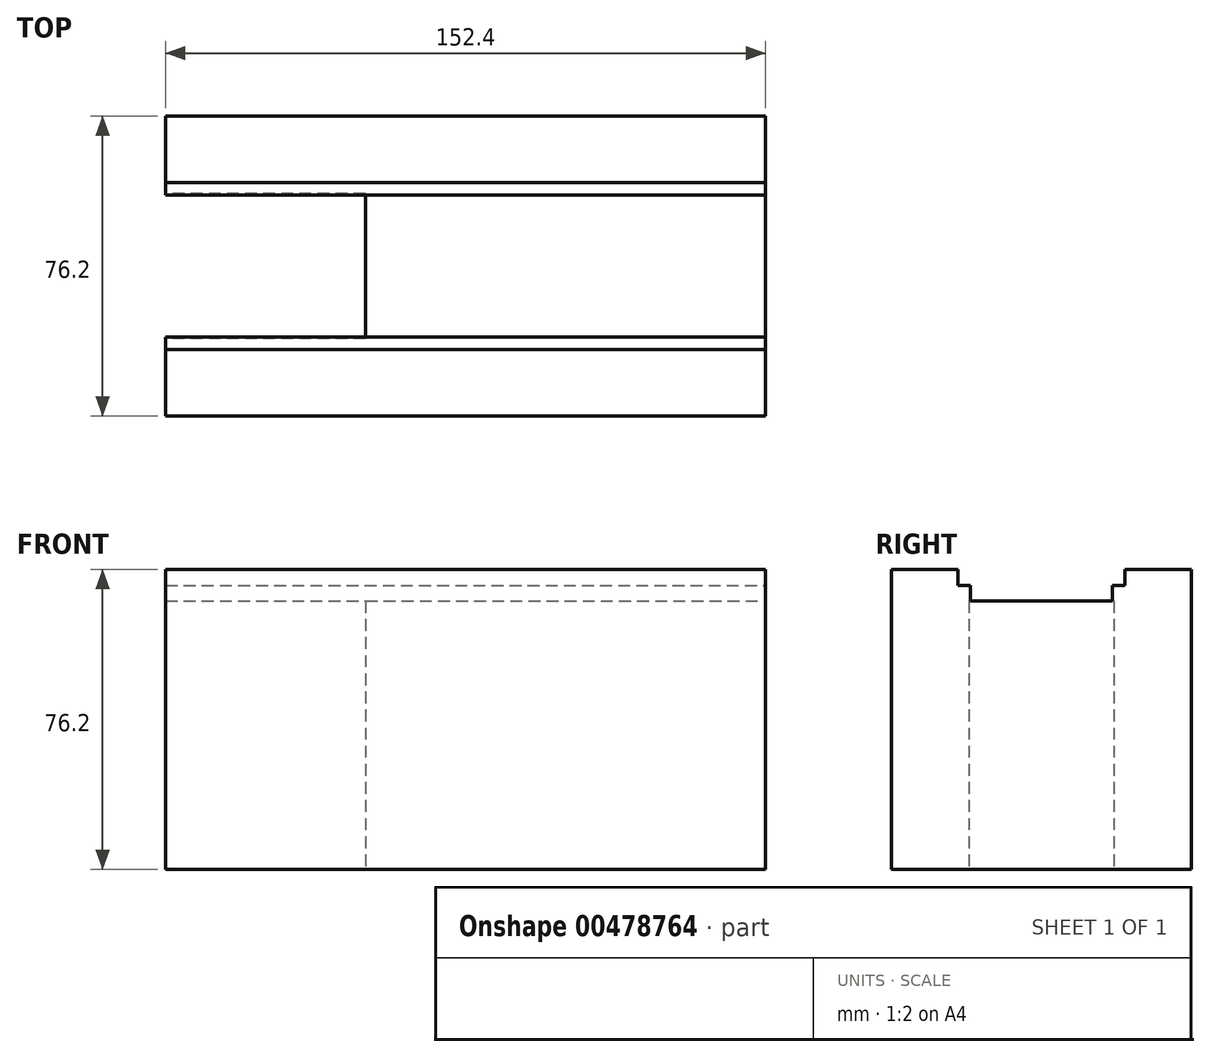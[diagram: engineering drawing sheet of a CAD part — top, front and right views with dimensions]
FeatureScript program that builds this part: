
annotation { "Feature Type Name" : "Feature", "Feature Type Description" : "" }
export const myFeature = defineFeature(function(context is Context, id is Id, definition is map)
    precondition{}
    {
        {
            var Q0;
            Q0=qCreatedBy(makeId("Right.planeOp"),FACE);
            var sketch = newSketch(context, id + "F0", { "sketchPlane" : qUnion([Q0])});
            skLineSegment(sketch, "E0.bottom", {"start": v(0, 0) * mm, "end": v(76.2, 0) * mm});
            skLineSegment(sketch, "E0.top", {"start": v(0, 76.2) * mm, "end": v(76.2, 76.2) * mm});
            skLineSegment(sketch, "E0.left", {"start": v(0, 0) * mm, "end": v(0, 76.2) * mm});
            skLineSegment(sketch, "E0.right", {"start": v(76.2, 0) * mm, "end": v(76.2, 76.2) * mm});
            skSolve(sketch);
        }
        {
            var Q0;
            Q0 = qSketchRegion(id + "F0", true);
            extrude(context, id + "F1", {"entities" : qUnion([Q0]), "depth" : 152.4 * mm});
        }
        {
            var Q0;
            Q0=makeQuery(id+"F1.opExtrude","CAP_FACE",FACE,{"disambiguationData":[OSD([sQuery(id+"F0.wireOp",EDGE,"E0.bottom"),sQuery(id+"F0.wireOp",EDGE,"E0.top"),sQuery(id+"F0.wireOp",EDGE,"E0.left"),sQuery(id+"F0.wireOp",EDGE,"E0.right")])],"isStart":false});
            var sketch = newSketch(context, id + "F2", { "sketchPlane" : qUnion([Q0])});
            skLineSegment(sketch, "E1.top", {"start": v(20.07, 68.2) * mm, "end": v(56.13, 68.2) * mm});
            skLineSegment(sketch, "E1.left", {"start": v(20.07, 76.2) * mm, "end": v(20.07, 68.2) * mm});
            skLineSegment(sketch, "E1.right", {"start": v(56.13, 76.2) * mm, "end": v(56.13, 68.2) * mm});
            skPoint(sketch, "E2", {"position": v(38.1, 68.2) * mm});
            skPoint(sketch, "E3", {"position": v(38.1, 76.2) * mm});
            skSolve(sketch);
        }
        {
            var Q0;
            Q0=makeQuery(id+"F2.imprint","IMPRINT",FACE,{"disambiguationData":[TD([[makeQuery(id+"F2.imprint","IMPRINT",EDGE,{"derivedFrom":sQuery(id+"F2.wireOp",EDGE,"E1.top")}),1.0]])]});
            extrude(context, id + "F3", {"entities" : qUnion([Q0]), "operationType" : NewBodyOperationType.REMOVE, "endBound" : BoundingType.THROUGH_ALL, "oppositeDirection" : true, "depth" : 152.4 * mm});
        }
        {
            var Q0;
            Q0=makeQuery(id+"F1.opExtrude","CAP_FACE",FACE,{"disambiguationData":[OSD([sQuery(id+"F0.wireOp",EDGE,"E0.bottom"),sQuery(id+"F0.wireOp",EDGE,"E0.top"),sQuery(id+"F0.wireOp",EDGE,"E0.left"),sQuery(id+"F0.wireOp",EDGE,"E0.right")])],"isStart":false});
            var sketch = newSketch(context, id + "F4", { "sketchPlane" : qUnion([Q0])});
            skLineSegment(sketch, "E4.bottom", {"start": v(16.9, 76.2) * mm, "end": v(20.07, 76.2) * mm});
            skLineSegment(sketch, "E4.top", {"start": v(16.9, 72.2) * mm, "end": v(20.07, 72.2) * mm});
            skLineSegment(sketch, "E4.left", {"start": v(16.9, 76.2) * mm, "end": v(16.9, 72.2) * mm});
            skLineSegment(sketch, "E4.right", {"start": v(20.07, 76.2) * mm, "end": v(20.07, 72.2) * mm});
            skLineSegment(sketch, "E5.bottom", {"start": v(56.13, 76.2) * mm, "end": v(59.3, 76.2) * mm});
            skLineSegment(sketch, "E5.top", {"start": v(56.13, 72.2) * mm, "end": v(59.3, 72.2) * mm});
            skLineSegment(sketch, "E5.left", {"start": v(56.13, 76.2) * mm, "end": v(56.13, 72.2) * mm});
            skLineSegment(sketch, "E5.right", {"start": v(59.3, 76.2) * mm, "end": v(59.3, 72.2) * mm});
            skSolve(sketch);
        }
        {
            var Q0;
            Q0=makeQuery(id+"F4.imprint","IMPRINT",FACE,{"disambiguationData":[TD([[makeQuery(id+"F4.imprint","IMPRINT",EDGE,{"derivedFrom":sQuery(id+"F4.wireOp",EDGE,"E4.bottom")}),-1.0]])]});
            var Q1;
            Q1=makeQuery(id+"F4.imprint","IMPRINT",FACE,{"disambiguationData":[TD([[makeQuery(id+"F4.imprint","IMPRINT",EDGE,{"derivedFrom":sQuery(id+"F4.wireOp",EDGE,"E5.bottom")}),-1.0]])]});
            extrude(context, id + "F5", {"entities" : qUnion([Q0, Q1]), "operationType" : NewBodyOperationType.REMOVE, "endBound" : BoundingType.THROUGH_ALL, "oppositeDirection" : true, "depth" : 101.6 * mm});
        }
        {
            var Q0;
            Q0=makeQuery(id+"F1.opExtrude","CAP_FACE",FACE,{"disambiguationData":[OSD([sQuery(id+"F0.wireOp",EDGE,"E0.bottom"),sQuery(id+"F0.wireOp",EDGE,"E0.top"),sQuery(id+"F0.wireOp",EDGE,"E0.left"),sQuery(id+"F0.wireOp",EDGE,"E0.right")])],"isStart":true});
            var sketch = newSketch(context, id + "F6", { "sketchPlane" : qUnion([Q0])});
            skLineSegment(sketch, "E6.bottom", {"start": v(-56.51, 68.2) * mm, "end": v(-19.69, 68.2) * mm});
            skLineSegment(sketch, "E6.top", {"start": v(-56.51, 0) * mm, "end": v(-19.68, 0) * mm});
            skLineSegment(sketch, "E6.left", {"start": v(-56.51, 68.2) * mm, "end": v(-56.51, 0) * mm});
            skLineSegment(sketch, "E6.right", {"start": v(-19.68, 68.2) * mm, "end": v(-19.68, 0) * mm});
            skLineSegment(sketch, "E7", {"start": v(-38.1, 68.2) * mm, "end": v(-38.1, 0) * mm, "construction": true});
            skPoint(sketch, "E8", {"position": v(-38.1, 68.2) * mm});
            skSolve(sketch);
        }
        {
            var Q0;
            Q0 = qSketchRegion(id + "F6", true);
            extrude(context, id + "F7", {"entities" : qUnion([Q0]), "operationType" : NewBodyOperationType.REMOVE, "oppositeDirection" : true, "depth" : 50.8 * mm});
        }
    });
